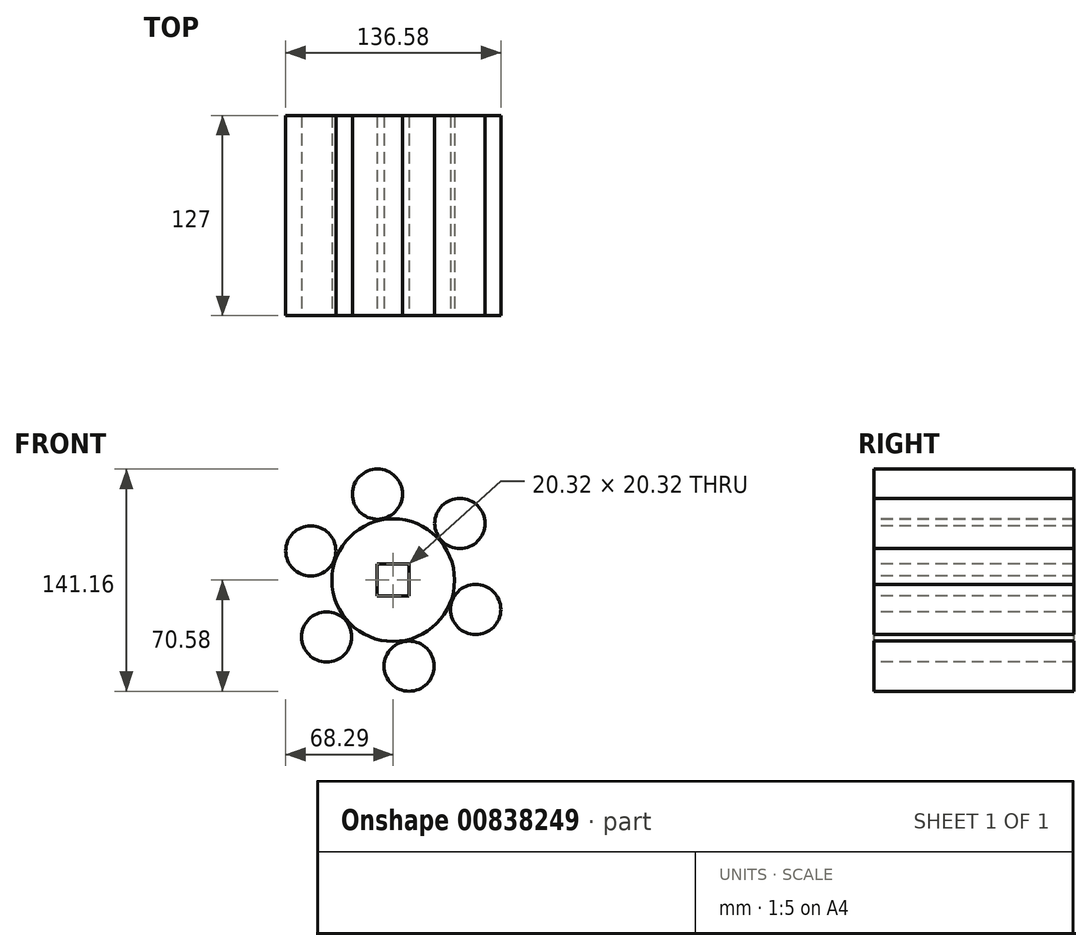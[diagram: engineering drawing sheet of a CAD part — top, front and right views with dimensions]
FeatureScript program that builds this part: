
annotation { "Feature Type Name" : "Feature", "Feature Type Description" : "" }
export const myFeature = defineFeature(function(context is Context, id is Id, definition is map)
    precondition{}
    {
        {
            var Q0;
            Q0=qCreatedBy(makeId("Front.planeOp"),FACE);
            var sketch = newSketch(context, id + "F0", { "sketchPlane" : qUnion([Q0])});
            skCircle(sketch, "E0", {"center": v(0, 0) * mm, "radius": 38.95 * mm});
            skCircle(sketch, "E1", {"center": v(0, 0) * mm, "radius": 26.72 * mm});
            skCircle(sketch, "E2", {"center": v(-10.07, 54.65) * mm, "radius": 15.94 * mm});
            skLineSegment(sketch, "E3", {"start": v(0, 0) * mm, "end": v(-10.07, 54.65) * mm, "construction": true});
            skCircle(sketch, "E4.1.0", {"center": v(-52.36, 18.6) * mm, "radius": 15.94 * mm});
            skCircle(sketch, "E4.2.0", {"center": v(-42.3, -36.04) * mm, "radius": 15.94 * mm});
            skCircle(sketch, "E4.3.0", {"center": v(10.07, -54.65) * mm, "radius": 15.94 * mm});
            skCircle(sketch, "E4.4.0", {"center": v(52.36, -18.6) * mm, "radius": 15.94 * mm});
            skCircle(sketch, "E4.5.0", {"center": v(42.3, 36.04) * mm, "radius": 15.94 * mm});
            skSolve(sketch);
        }
        {
            var Q0;
            Q0=makeQuery(id+"F0.imprint","IMPRINT",FACE,{"disambiguationData":[TD([[makeQuery(id+"F0.imprint","IMPRINT",EDGE,{"derivedFrom":sQuery(id+"F0.wireOp",EDGE,"E4.5.0")}),1.0]])]});
            var Q1;
            Q1=makeQuery(id+"F0.imprint","IMPRINT",FACE,{"disambiguationData":[TD([[makeQuery(id+"F0.imprint","IMPRINT",EDGE,{"derivedFrom":sQuery(id+"F0.wireOp",EDGE,"E0")}),1.0]])]});
            var Q2;
            Q2=makeQuery(id+"F0.imprint","IMPRINT",FACE,{"disambiguationData":[TD([[makeQuery(id+"F0.imprint","IMPRINT",EDGE,{"derivedFrom":sQuery(id+"F0.wireOp",EDGE,"E1")}),1.0]])]});
            var Q3;
            Q3=makeQuery(id+"F0.imprint","IMPRINT",FACE,{"disambiguationData":[TD([[makeQuery(id+"F0.imprint","IMPRINT",EDGE,{"derivedFrom":sQuery(id+"F0.wireOp",EDGE,"E2")}),1.0]])]});
            var Q4;
            Q4=makeQuery(id+"F0.imprint","IMPRINT",FACE,{"disambiguationData":[TD([[makeQuery(id+"F0.imprint","IMPRINT",EDGE,{"derivedFrom":sQuery(id+"F0.wireOp",EDGE,"E4.1.0")}),1.0]])]});
            var Q5;
            Q5=makeQuery(id+"F0.imprint","IMPRINT",FACE,{"disambiguationData":[TD([[makeQuery(id+"F0.imprint","IMPRINT",EDGE,{"derivedFrom":sQuery(id+"F0.wireOp",EDGE,"E4.2.0")}),1.0]])]});
            var Q6;
            Q6=makeQuery(id+"F0.imprint","IMPRINT",FACE,{"disambiguationData":[TD([[makeQuery(id+"F0.imprint","IMPRINT",EDGE,{"derivedFrom":sQuery(id+"F0.wireOp",EDGE,"E4.3.0")}),1.0]])]});
            var Q7;
            Q7=makeQuery(id+"F0.imprint","IMPRINT",FACE,{"disambiguationData":[TD([[makeQuery(id+"F0.imprint","IMPRINT",EDGE,{"derivedFrom":sQuery(id+"F0.wireOp",EDGE,"E4.4.0")}),1.0]])]});
            extrude(context, id + "F1", {"entities" : qUnion([Q0, Q1, Q2, Q3, Q4, Q5, Q6, Q7]), "endBound" : BoundingType.SYMMETRIC, "oppositeDirection" : true, "depth" : 127 * mm, "offsetDistance" : 25.4 * mm});
        }
        {
            var Q0;
            Q0=qCreatedBy(makeId("Front.planeOp"),FACE);
            var sketch = newSketch(context, id + "F2", { "sketchPlane" : qUnion([Q0])});
            skLineSegment(sketch, "E5.bottom", {"start": v(23.26, -20.32) * mm, "end": v(-23.26, -20.32) * mm});
            skLineSegment(sketch, "E5.top", {"start": v(23.26, 20.32) * mm, "end": v(-23.26, 20.32) * mm});
            skLineSegment(sketch, "E5.left", {"start": v(23.26, -20.32) * mm, "end": v(23.26, 20.32) * mm});
            skLineSegment(sketch, "E5.right", {"start": v(-23.26, -20.32) * mm, "end": v(-23.26, 20.32) * mm});
            skPoint(sketch, "E5.middle", {"position": v(0, 0) * mm});
            skLineSegment(sketch, "E6.bottom", {"start": v(6.34, -26.9) * mm, "end": v(-0.23, -26.9) * mm});
            skLineSegment(sketch, "E6.top", {"start": v(6.34, -25.02) * mm, "end": v(-0.23, -25.02) * mm});
            skLineSegment(sketch, "E6.left", {"start": v(6.34, -26.9) * mm, "end": v(6.34, -25.02) * mm});
            skLineSegment(sketch, "E6.right", {"start": v(-0.23, -26.9) * mm, "end": v(-0.23, -25.02) * mm});
            skPoint(sketch, "E6.middle", {"position": v(3.05, -25.96) * mm});
            skSolve(sketch);
        }
        {
            var Q0;
            Q0=sQuery(id+"F2.wireOp",EDGE,"E5.left");
            var Q1;
            Q1=sQuery(id+"F2.wireOp",EDGE,"E5.right");
            extrude(context, id + "F3", {"bodyType" : ToolBodyType.SURFACE, "surfaceEntities" : qUnion([Q0, Q1]), "endBound" : BoundingType.THROUGH_ALL, "oppositeDirection" : true, "depth" : 25.4 * mm, "offsetDistance" : 25.4 * mm});
        }
        {
            var Q0;
            Q0=makeQuery(id+"F3.opExtrude","SWEPT_FACE",FACE,{"disambiguationData":[OSD([sQuery(id+"F2.wireOp",EDGE,"E5.left")])]});
            var sketch = newSketch(context, id + "F4", { "sketchPlane" : qUnion([Q0])});
            skLineSegment(sketch, "E7", {"start": v(-66.2, 0) * mm, "end": v(-236.76, 0) * mm});
            skLineSegment(sketch, "E8", {"start": v(-98.8, 0) * mm, "end": v(-239.3, 0) * mm, "construction": true});
            skLineSegment(sketch, "E9.bottom", {"start": v(-170.31, -7.75) * mm, "end": v(-70.31, -7.75) * mm});
            skLineSegment(sketch, "E9.top", {"start": v(-170.31, 7.75) * mm, "end": v(-70.31, 7.75) * mm});
            skLineSegment(sketch, "E9.left", {"start": v(-170.31, -7.75) * mm, "end": v(-170.31, 7.75) * mm});
            skLineSegment(sketch, "E9.right", {"start": v(-70.31, -7.75) * mm, "end": v(-70.31, 7.75) * mm});
            skPoint(sketch, "E9.middle", {"position": v(-120.31, 0) * mm});
            skLineSegment(sketch, "E10.bottom", {"start": v(-208.92, 0) * mm, "end": v(-131.7, 0) * mm});
            skLineSegment(sketch, "E10.top", {"start": v(-208.92, 0) * mm, "end": v(-131.7, 0) * mm});
            skLineSegment(sketch, "E10.left", {"start": v(-208.92, 0) * mm, "end": v(-208.92, 0) * mm});
            skLineSegment(sketch, "E10.right", {"start": v(-131.7, 0) * mm, "end": v(-131.7, 0) * mm});
            skPoint(sketch, "E10.middle", {"position": v(-170.31, 0) * mm});
            skPoint(sketch, "E11.middle", {"position": v(-170.31, 7.75) * mm});
            skSolve(sketch);
        }
        {
            var Q0;
            {var subQ1=sQuery(id+"F4.wireOp",EDGE,"E9.top");Q0=makeQuery(id+"F4.imprint","IMPRINT",FACE,{"disambiguationData":[TD([[makeQuery(id+"F4.imprint","IMPRINT",EDGE,{"derivedFrom":subQ1}),-1.0]])]});}
            var Q1;
            {var subQ1=sQuery(id+"F4.wireOp",EDGE,"E9.bottom");Q1=makeQuery(id+"F4.imprint","IMPRINT",FACE,{"disambiguationData":[TD([[makeQuery(id+"F4.imprint","IMPRINT",EDGE,{"derivedFrom":subQ1}),1.0]])]});}
            extrude(context, id + "F5", {"entities" : qUnion([Q0, Q1]), "operationType" : NewBodyOperationType.REMOVE, "oppositeDirection" : true, "depth" : 25.4 * mm, "offsetDistance" : 25.4 * mm});
        }
        {
            var Q0;
            Q0=makeQuery(id+"F3.opExtrude","SWEPT_FACE",FACE,{"disambiguationData":[OSD([sQuery(id+"F2.wireOp",EDGE,"E5.left")])]});
            var sketch = newSketch(context, id + "F6", { "sketchPlane" : qUnion([Q0])});
            skCircle(sketch, "E12", {"center": v(-105.67, 0) * mm, "radius": 12.01 * mm});
            skCircle(sketch, "E13.1.0.0", {"center": v(-147.58, 0) * mm, "radius": 12.01 * mm});
            skCircle(sketch, "E13.2.0.0", {"center": v(-189.49, 0) * mm, "radius": 12.01 * mm});
            skLineSegment(sketch, "E13.direction1", {"start": v(-105.67, 0) * mm, "end": v(-147.58, 0) * mm, "construction": true});
            skSolve(sketch);
        }
        {
            var Q0;
            Q0=makeQuery(id+"F6.imprint","IMPRINT",FACE,{"disambiguationData":[TD([[makeQuery(id+"F6.imprint","IMPRINT",EDGE,{"derivedFrom":sQuery(id+"F6.wireOp",EDGE,"E12")}),-1.0]])]});
            var Q1;
            Q1=sQuery(id+"F6.wireOp",EDGE,"E13.2.0.0");
            var Q2;
            Q2=sQuery(id+"F6.wireOp",EDGE,"E13.1.0.0");
            var Q3;
            Q3=sQuery(id+"F6.wireOp",EDGE,"E12");
            extrude(context, id + "F7", {"entities" : qUnion([Q0]), "bodyType" : ToolBodyType.SURFACE, "surfaceEntities" : qUnion([Q1, Q2, Q3]), "endBound" : BoundingType.UP_TO_NEXT, "depth" : 218.95 * mm, "offsetDistance" : 25.4 * mm});
        }
        {
            var Q0;
            Q0=makeQuery(id+"F1.opExtrude","CAP_FACE",FACE,{"disambiguationData":[OSD([sQuery(id+"F0.wireOp",EDGE,"E0")])],"isStart":true});
            var sketch = newSketch(context, id + "F8", { "sketchPlane" : qUnion([Q0])});
            skLineSegment(sketch, "E14.bottom", {"start": v(10.16, -10.16) * mm, "end": v(-10.16, -10.16) * mm});
            skLineSegment(sketch, "E14.top", {"start": v(10.16, 10.16) * mm, "end": v(-10.16, 10.16) * mm});
            skLineSegment(sketch, "E14.left", {"start": v(10.16, -10.16) * mm, "end": v(10.16, 10.16) * mm});
            skLineSegment(sketch, "E14.right", {"start": v(-10.16, -10.16) * mm, "end": v(-10.16, 10.16) * mm});
            skPoint(sketch, "E14.middle", {"position": v(0, 0) * mm});
            skSolve(sketch);
        }
        {
            var Q0;
            Q0=makeQuery(id+"F8.imprint","IMPRINT",FACE,{"disambiguationData":[TD([[makeQuery(id+"F8.imprint","IMPRINT",EDGE,{"derivedFrom":sQuery(id+"F8.wireOp",EDGE,"E14.bottom")}),-1.0]])]});
            extrude(context, id + "F9", {"entities" : qUnion([Q0]), "operationType" : NewBodyOperationType.REMOVE, "endBound" : BoundingType.THROUGH_ALL, "oppositeDirection" : true, "depth" : 25.4 * mm, "offsetDistance" : 25.4 * mm});
        }
    });
